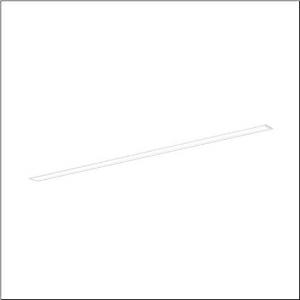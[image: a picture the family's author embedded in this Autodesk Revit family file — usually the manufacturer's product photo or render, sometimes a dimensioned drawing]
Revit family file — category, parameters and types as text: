
# Revit family: silica_r__21_51mx13tbt5w_c30f
name_source: partatom
category: Lighting Fixtures
units: mm (PartAtom-declared; Revit-internal decimal feet)

## family parameters
Cut with Voids When Loaded = No
Host = Face
Light Source = No
Part Type = Normal
Room Calculation Point = No
Round Connector Dimension = Use Diameter
Shared = No

## types (1)
- --- (1 x LED, 4030 lm, 40.5 W, 6500K)
    Apparent Load = 41 VA
    CIE Flux Codes = 78 96 99 100 100
    Color Rendering = 80
    Color Temperature = 6500K
    Default Elevation = 1800 mm
    Description = Silica® 21, office luminaire, primary optical cover: prismatic diffuser, of PMMA, CAT 2 (L<= 3000cd/m²), light emission: direct distribution, primary light characteristic: symmetric, installation type: recessed, LED, rated luminous flux: 4.030lm, luminous efficacy: 95lm/W, light colour: 8tw, colour temperature: 2700..6500K, control gear: DALI DT8, with terminal, 3+2-pole, max. 2.5mm², mains connection: 220..240V, AC, 50/60Hz, rated input power: 42.6W, luminaire housing, of aluminium, traffic white (RAL 9016), length: 1.528mm, width: 79mm, height: 53mm, protection rating (complete): IP20, insulation class (complete): insulation class I (protective earthing), certification: CE, ENEC, VDE, permissible operating ambient temperature: 0..+35°C, standard: EN 50419, packaging unit: 1 piece
    Height = 0 mm  [stored 0 ft]
    Lamp = 1 x LED
    Lamp Light Flux = 4030 lm
    Lamp Power = 40.5 W
    Lamp count = 1
    Length = 1527 mm
    Luminous efficacy = 100 lm/W
    Manufacturer = Siteco
    ModVariant = No
    Model = 51MX13TBT5W
    Mounting Place = Ceiling
    Mounting Type = Recessed
    Number of Poles = 1
    OnlyDefault = Yes
    Power Factor = 1
    Product Name = Silica® 21
    Product group = office luminaire | ceiling recessed
    ProductGroupID = 401
    Protection Class = Protection class I
    Protection Degree = IP 20
    RLX_Detail_Level = 1
    RLX_Emergency_Light_Flux = 0 lm
    RLX_Emergency_Type = 0
    RLX_Emergency_Type_DB = No
    RlxData = <blob elided: 10977 chars, md5=fabe60b3>
    Socket = socket
    Standby Power = 0 W
    System Light Flux = 4030 lm
    System Power = 41 W
    Type Comments = individual setting
    Type Image = l_1251692.jpg
    URL = http://relux.com
    VarID = @adj_139848
    Voltage = 0 V
    Weight = 0.00 kg
    Width = 79 mm

note: [stored X ft] marks values corroborated as IEEE doubles in the binary element streams (Revit-internal decimal feet)

## geometry (parser evidence)
native form markers: Sweep x12
no freeform markers — native parametric forms only
